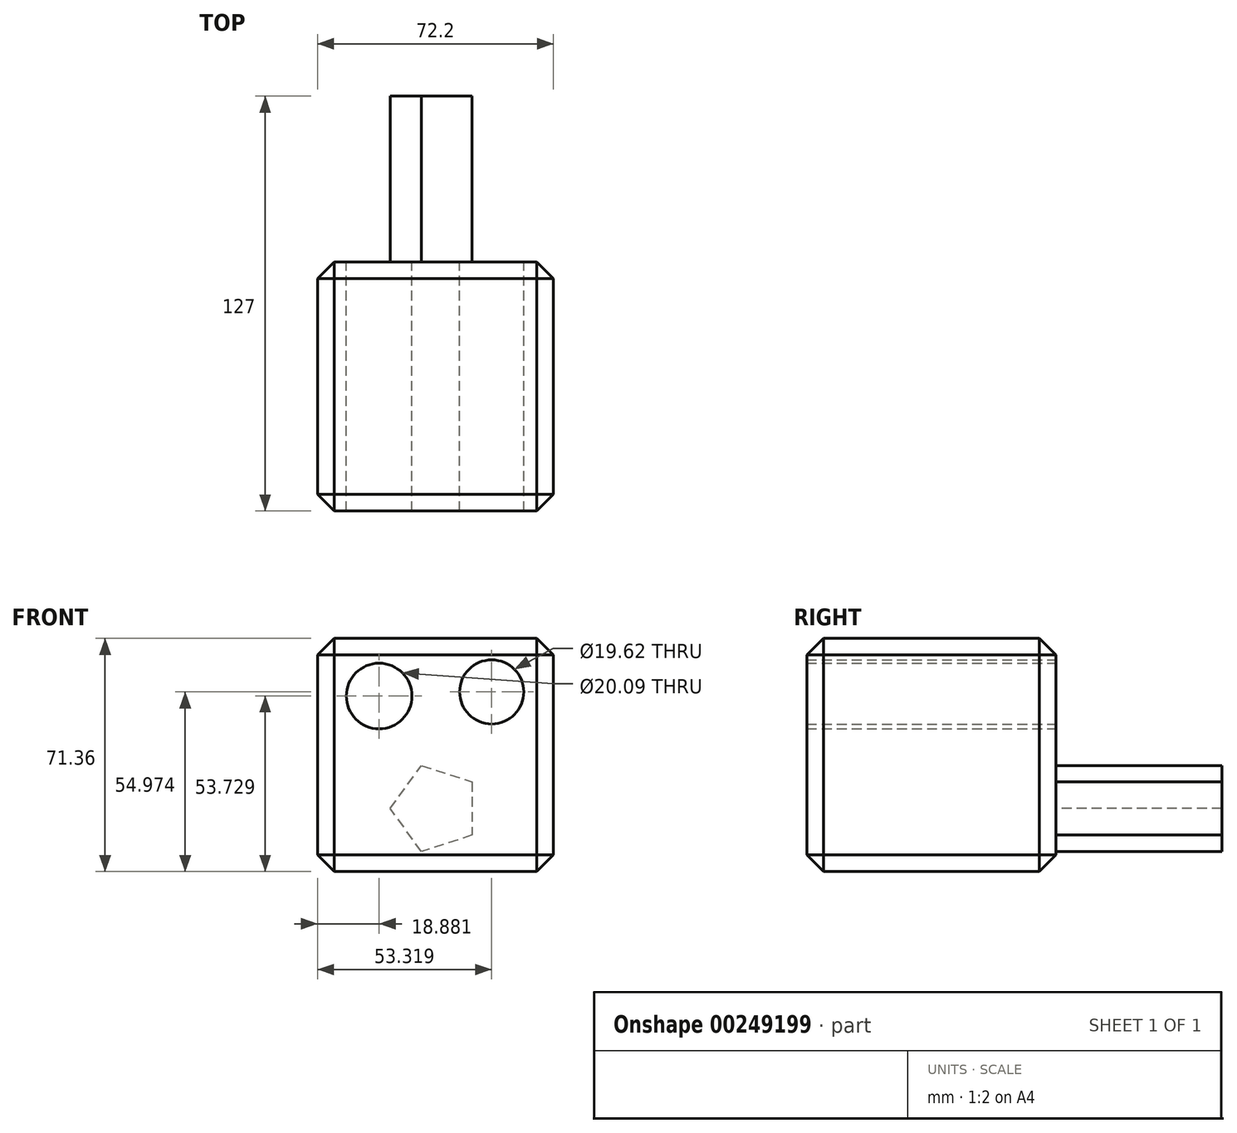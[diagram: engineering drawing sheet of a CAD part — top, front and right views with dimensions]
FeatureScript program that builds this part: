
annotation { "Feature Type Name" : "Feature", "Feature Type Description" : "" }
export const myFeature = defineFeature(function(context is Context, id is Id, definition is map)
    precondition{}
    {
        {
            var Q0;
            Q0=qCreatedBy(makeId("Front.planeOp"),FACE);
            var sketch = newSketch(context, id + "F0", { "sketchPlane" : qUnion([Q0])});
            skPoint(sketch, "E0.0", {"position": v(0, 0) * mm});
            skLineSegment(sketch, "E1.bottom", {"start": v(36.1, -35.68) * mm, "end": v(-36.1, -35.68) * mm});
            skLineSegment(sketch, "E1.top", {"start": v(36.1, 35.68) * mm, "end": v(-36.1, 35.68) * mm});
            skLineSegment(sketch, "E1.left", {"start": v(36.1, -35.68) * mm, "end": v(36.1, 35.68) * mm});
            skLineSegment(sketch, "E1.right", {"start": v(-36.1, -35.68) * mm, "end": v(-36.1, 35.68) * mm});
            skSolve(sketch);
        }
        {
            var Q0;
            Q0 = qSketchRegion(id + "F0", true);
            extrude(context, id + "F1", {"entities" : qUnion([Q0]), "depth" : 76.2 * mm});
        }
        {
            var Q0;
            Q0=makeQuery(id+"F1.opExtrude","CAP_FACE",FACE,{"disambiguationData":[OSD([sQuery(id+"F0.wireOp",EDGE,"E1.bottom"),sQuery(id+"F0.wireOp",EDGE,"E1.top"),sQuery(id+"F0.wireOp",EDGE,"E1.left"),sQuery(id+"F0.wireOp",EDGE,"E1.right")])],"isStart":false});
            var Q1;
            Q1=makeQuery(id+"F1.opExtrude","SWEPT_FACE",FACE,{"disambiguationData":[OSD([sQuery(id+"F0.wireOp",EDGE,"E1.left")])]});
            var Q2;
            Q2=makeQuery(id+"F1.opExtrude","SWEPT_FACE",FACE,{"disambiguationData":[OSD([sQuery(id+"F0.wireOp",EDGE,"E1.top")])]});
            var Q3;
            Q3=makeQuery(id+"F1.opExtrude","SWEPT_FACE",FACE,{"disambiguationData":[OSD([sQuery(id+"F0.wireOp",EDGE,"E1.right")])]});
            var Q4;
            Q4=makeQuery(id+"F1.opExtrude","SWEPT_FACE",FACE,{"disambiguationData":[OSD([sQuery(id+"F0.wireOp",EDGE,"E1.bottom")])]});
            chamfer(context, id + "F2", {"entities" : qUnion([Q0, Q1, Q2, Q3, Q4]), "width" : 5.08 * mm, "tangentPropagation" : true});
        }
        {
            var Q0;
            Q0=qCreatedBy(makeId("Front.planeOp"),FACE);
            var sketch = newSketch(context, id + "F3", { "sketchPlane" : qUnion([Q0])});
            skCircle(sketch, "E2", {"center": v(-17.22, 18.05) * mm, "radius": 10.04 * mm});
            skCircle(sketch, "E3", {"center": v(17.22, 19.3) * mm, "radius": 9.81 * mm});
            skSolve(sketch);
        }
        {
            var Q0;
            Q0 = qSketchRegion(id + "F3", true);
            extrude(context, id + "F4", {"entities" : qUnion([Q0]), "operationType" : NewBodyOperationType.REMOVE, "depth" : 76.2 * mm});
        }
        {
            var Q0;
            Q0=qCreatedBy(makeId("Front.planeOp"),FACE);
            var sketch = newSketch(context, id + "F5", { "sketchPlane" : qUnion([Q0])});
            skCircle(sketch, "E4.cCircle", {"center": v(0, -16.39) * mm, "radius": 11.2 * mm, "construction": true});
            skLineSegment(sketch, "E4.0", {"start": v(11.2, -8.25) * mm, "end": v(11.2, -24.53) * mm});
            skLineSegment(sketch, "E4.1", {"start": v(11.2, -24.53) * mm, "end": v(-4.28, -29.56) * mm});
            skLineSegment(sketch, "E4.2", {"start": v(-4.28, -29.56) * mm, "end": v(-13.85, -16.39) * mm});
            skLineSegment(sketch, "E4.3", {"start": v(-13.85, -16.39) * mm, "end": v(-4.28, -3.22) * mm});
            skLineSegment(sketch, "E4.4", {"start": v(-4.28, -3.22) * mm, "end": v(11.2, -8.25) * mm});
            skPoint(sketch, "E4.0.midPoint", {"position": v(11.2, -16.39) * mm});
            skSolve(sketch);
        }
        {
            var Q0;
            Q0 = qSketchRegion(id + "F5", true);
            extrude(context, id + "F6", {"entities" : qUnion([Q0]), "operationType" : NewBodyOperationType.ADD, "oppositeDirection" : true, "depth" : 50.8 * mm});
        }
    });
